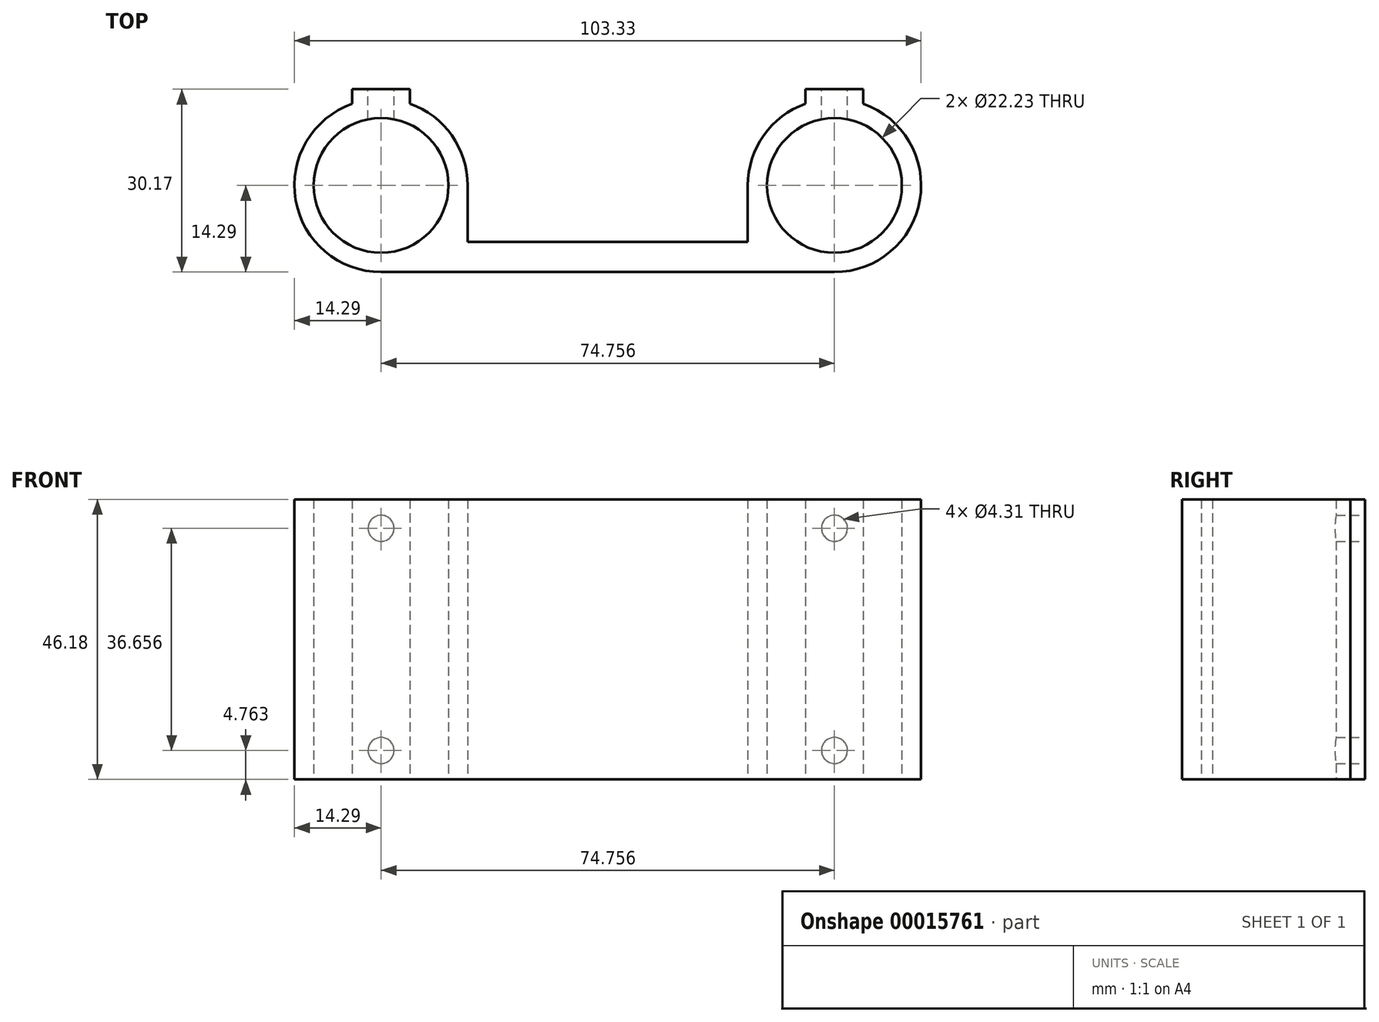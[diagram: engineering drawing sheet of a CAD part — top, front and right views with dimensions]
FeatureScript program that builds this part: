
annotation { "Feature Type Name" : "Feature", "Feature Type Description" : "" }
export const myFeature = defineFeature(function(context is Context, id is Id, definition is map)
    precondition{}
    {
        {
            var Q0;
            Q0=qCreatedBy(makeId("Top.planeOp"),FACE);
            var sketch = newSketch(context, id + "F0", { "sketchPlane" : qUnion([Q0])});
            skCircle(sketch, "E0", {"center": v(0, 0) * mm, "radius": 11.11 * mm});
            skLineSegment(sketch, "E1", {"start": v(0, 0) * mm, "end": v(0, 13.47) * mm, "construction": true});
            skLineSegment(sketch, "E2", {"start": v(-4.76, 13.47) * mm, "end": v(4.76, 13.47) * mm, "construction": true});
            skArc(sketch, "E3", {"start": v(-4.76, 13.47) * mm, "mid": v(-14.08, -2.42) * mm, "end": v(0, -14.29) * mm});
            skArc(sketch, "E4", {"start": v(14.29, 0) * mm, "mid": v(11.67, 8.25) * mm, "end": v(4.76, 13.47) * mm});
            skLineSegment(sketch, "E5.top", {"start": v(14.29, -9.29) * mm, "end": v(60.47, -9.29) * mm});
            skLineSegment(sketch, "E5.left", {"start": v(14.29, 0) * mm, "end": v(14.29, -9.29) * mm});
            skLineSegment(sketch, "E5.right", {"start": v(60.47, 0) * mm, "end": v(60.47, -9.29) * mm});
            skArc(sketch, "E6", {"start": v(70, 13.47) * mm, "mid": v(63.1, 8.25) * mm, "end": v(60.47, 0) * mm});
            skLineSegment(sketch, "E7", {"start": v(70, 13.47) * mm, "end": v(79.52, 13.47) * mm, "construction": true});
            skLineSegment(sketch, "E8", {"start": v(74.76, 13.47) * mm, "end": v(74.76, 0) * mm, "construction": true});
            skArc(sketch, "E9", {"start": v(74.76, -14.29) * mm, "mid": v(88.84, -2.42) * mm, "end": v(79.52, 13.47) * mm});
            skLineSegment(sketch, "E10", {"start": v(0, -14.29) * mm, "end": v(74.76, -14.29) * mm});
            skLineSegment(sketch, "E11", {"start": v(37.38, -14.29) * mm, "end": v(37.38, -9.29) * mm});
            skCircle(sketch, "E12", {"center": v(74.76, 0) * mm, "radius": 11.11 * mm});
            skLineSegment(sketch, "E13.top", {"start": v(-4.76, 15.88) * mm, "end": v(4.76, 15.88) * mm});
            skLineSegment(sketch, "E13.left", {"start": v(-4.76, 13.47) * mm, "end": v(-4.76, 15.88) * mm});
            skLineSegment(sketch, "E13.right", {"start": v(4.76, 13.47) * mm, "end": v(4.76, 15.88) * mm});
            skLineSegment(sketch, "E14.top", {"start": v(70, 15.88) * mm, "end": v(79.52, 15.88) * mm});
            skLineSegment(sketch, "E14.left", {"start": v(70, 13.47) * mm, "end": v(70, 15.88) * mm});
            skLineSegment(sketch, "E14.right", {"start": v(79.52, 13.47) * mm, "end": v(79.52, 15.88) * mm});
            skSolve(sketch);
        }
        {
            var Q0;
            Q0 = qSketchRegion(id + "F0", true);
            extrude(context, id + "F1", {"entities" : qUnion([Q0]), "depth" : 46.18 * mm});
        }
        {
            var Q0;
            Q0=makeQuery(id+"F1.opExtrude","SWEPT_FACE",FACE,{"disambiguationData":[OSD([sQuery(id+"F0.wireOp",EDGE,"E13.top")])]});
            var sketch = newSketch(context, id + "F2", { "sketchPlane" : qUnion([Q0])});
            skLineSegment(sketch, "E15", {"start": v(-4.76, 23.1) * mm, "end": v(-70, 23.1) * mm, "construction": true});
            skLineSegment(sketch, "E16.bottom", {"start": v(0, 0) * mm, "end": v(4.76, 0) * mm, "construction": true});
            skLineSegment(sketch, "E16.top", {"start": v(0, 4.76) * mm, "end": v(4.76, 4.76) * mm, "construction": true});
            skLineSegment(sketch, "E16.left", {"start": v(0, 0) * mm, "end": v(0, 4.76) * mm, "construction": true});
            skLineSegment(sketch, "E16.right", {"start": v(4.76, 0) * mm, "end": v(4.76, 4.76) * mm, "construction": true});
            skLineSegment(sketch, "E17.bottom", {"start": v(0, 4.76) * mm, "end": v(-74.76, 4.76) * mm, "construction": true});
            skLineSegment(sketch, "E17.top", {"start": v(0, 41.42) * mm, "end": v(-74.76, 41.42) * mm, "construction": true});
            skLineSegment(sketch, "E17.left", {"start": v(0, 4.76) * mm, "end": v(0, 41.42) * mm, "construction": true});
            skLineSegment(sketch, "E17.right", {"start": v(-74.76, 4.76) * mm, "end": v(-74.76, 41.42) * mm, "construction": true});
            skPoint(sketch, "E17.middle", {"position": v(-37.38, 23.1) * mm});
            skCircle(sketch, "E18", {"center": v(0, 4.76) * mm, "radius": 2.15 * mm});
            skCircle(sketch, "E19", {"center": v(-74.76, 4.76) * mm, "radius": 2.15 * mm});
            skCircle(sketch, "E20", {"center": v(-74.76, 41.42) * mm, "radius": 2.15 * mm});
            skCircle(sketch, "E21", {"center": v(0, 41.42) * mm, "radius": 2.15 * mm});
            skSolve(sketch);
        }
        {
            var Q0;
            Q0 = qSketchRegion(id + "F2", true);
            var Q1;
            Q1=makeQuery(id+"F1.opExtrude","SWEPT_FACE",FACE,{"disambiguationData":[OSD([sQuery(id+"F0.wireOp",EDGE,"E12")])]});
            extrude(context, id + "F3", {"entities" : qUnion([Q0]), "operationType" : NewBodyOperationType.REMOVE, "oppositeDirection" : true, "endBoundEntityFace" : qUnion([Q1]), "depth" : 6.35 * mm});
        }
    });
